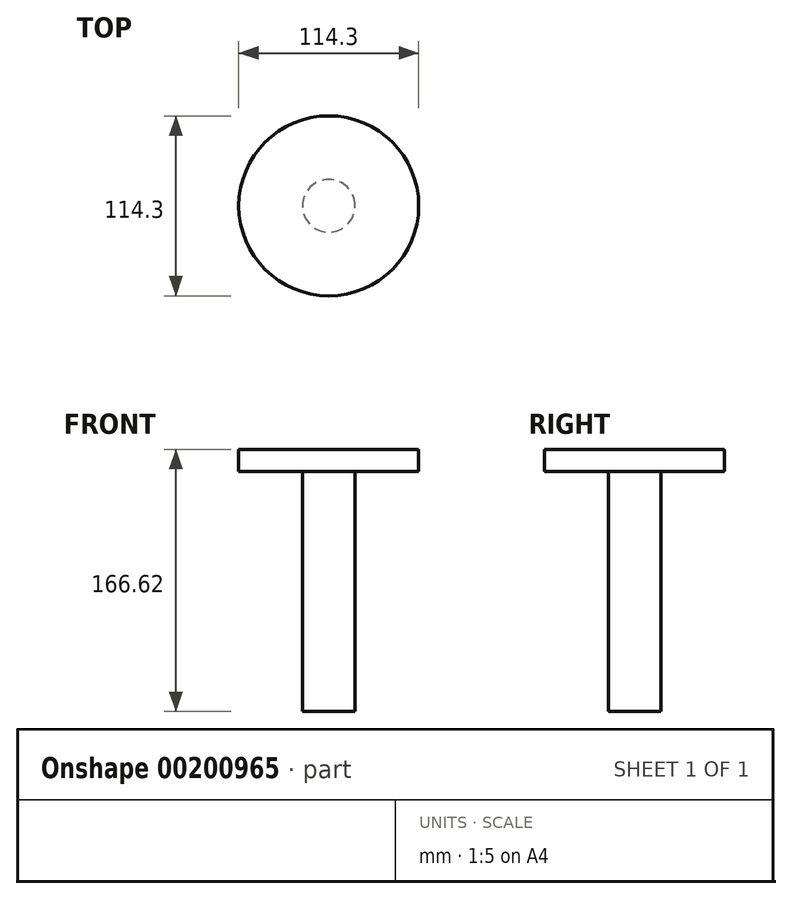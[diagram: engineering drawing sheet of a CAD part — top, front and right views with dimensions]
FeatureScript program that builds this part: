
annotation { "Feature Type Name" : "Feature", "Feature Type Description" : "" }
export const myFeature = defineFeature(function(context is Context, id is Id, definition is map)
    precondition{}
    {
        {
            var Q0;
            Q0=qCreatedBy(makeId("Front.planeOp"),FACE);
            var sketch = newSketch(context, id + "F0", { "sketchPlane" : qUnion([Q0])});
            skLineSegment(sketch, "E0", {"start": v(0, 0) * mm, "end": v(0, 335.65) * mm});
            skLineSegment(sketch, "E1", {"start": v(0, 0) * mm, "end": v(0, 166.62) * mm});
            skLineSegment(sketch, "E2", {"start": v(0, 166.62) * mm, "end": v(57.15, 166.62) * mm});
            skLineSegment(sketch, "E3", {"start": v(57.15, 166.62) * mm, "end": v(57.15, 152.4) * mm});
            skLineSegment(sketch, "E4", {"start": v(57.15, 152.4) * mm, "end": v(16.69, 152.4) * mm});
            skLineSegment(sketch, "E5", {"start": v(16.69, 152.4) * mm, "end": v(16.69, 0) * mm});
            skLineSegment(sketch, "E6", {"start": v(16.69, 0) * mm, "end": v(0, 0) * mm});
            skSolve(sketch);
        }
        {
            var Q0;
            {var subQ0=sQuery(id+"F0.wireOp",EDGE,"E2");Q0=makeQuery(id+"F0.imprint","IMPRINT",FACE,{"disambiguationData":[TD([[makeQuery(id+"F0.imprint","IMPRINT",EDGE,{"derivedFrom":subQ0}),-1.0]])]});}
            var Q1;
            Q1=sQuery(id+"F0.wireOp",EDGE,"E0");
            revolve(context, id + "F1", {"surfaceOperationType" : NewSurfaceOperationType.NEW, "entities" : qUnion([Q0]), "axis" : qUnion([Q1]), "revolveType" : RevolveType.FULL});
        }
    });
